annotation { "Feature Type Name" : "Feature", "Feature Type Description" : "" }
export const myFeature = defineFeature(function(context is Context, id is Id, definition is map)
    precondition{}
    {
        {
            var Q0;
            Q0=qCreatedBy(makeId("Top.planeOp"),FACE);
            var sketch = newSketch(context, id + "F0", { "sketchPlane" : qUnion([Q0])});
            skLineSegment(sketch, "E0.bottom", {"start": v(0, 0) * mm, "end": v(19.05, 0) * mm});
            skLineSegment(sketch, "E0.top", {"start": v(0, -63.5) * mm, "end": v(19.05, -63.5) * mm});
            skLineSegment(sketch, "E0.left", {"start": v(0, 0) * mm, "end": v(0, -63.5) * mm});
            skLineSegment(sketch, "E0.right", {"start": v(19.05, 0) * mm, "end": v(19.05, -63.5) * mm});
            skSolve(sketch);
        }
        {
            var Q0;
            Q0=makeQuery(id+"F0.imprint","IMPRINT",FACE,{"disambiguationData":[TD([[makeQuery(id+"F0.imprint","IMPRINT",EDGE,{"derivedFrom":sQuery(id+"F0.wireOp",EDGE,"E0.bottom")}),-1.0]])]});
            extrude(context, id + "F1", {"entities" : qUnion([Q0]), "depth" : 3.8 * mm, "offsetDistance" : 25.4 * mm});
        }
        {
            var Q0;
            Q0=makeQuery(id+"F1.opExtrude","CAP_FACE",FACE,{"disambiguationData":[OSD([sQuery(id+"F0.wireOp",EDGE,"E0.bottom"),sQuery(id+"F0.wireOp",EDGE,"E0.top"),sQuery(id+"F0.wireOp",EDGE,"E0.left"),sQuery(id+"F0.wireOp",EDGE,"E0.right")])],"isStart":false});
            var sketch = newSketch(context, id + "F2", { "sketchPlane" : qUnion([Q0])});
            skLineSegment(sketch, "E1", {"start": v(9.24, -2.12) * mm, "end": v(9.11, -2.05) * mm});
            skLineSegment(sketch, "E2", {"start": v(9.11, -2.05) * mm, "end": v(8.91, -1.97) * mm});
            skLineSegment(sketch, "E3", {"start": v(8.91, -1.97) * mm, "end": v(8.7, -1.89) * mm});
            skLineSegment(sketch, "E4", {"start": v(8.7, -1.89) * mm, "end": v(8.49, -1.82) * mm});
            skLineSegment(sketch, "E5", {"start": v(8.49, -1.82) * mm, "end": v(8.31, -1.76) * mm});
            skLineSegment(sketch, "E6", {"start": v(8.31, -1.76) * mm, "end": v(8.15, -1.7) * mm});
            skLineSegment(sketch, "E7", {"start": v(8.15, -1.7) * mm, "end": v(7.89, -1.66) * mm});
            skLineSegment(sketch, "E8", {"start": v(7.89, -1.66) * mm, "end": v(7.46, -1.56) * mm});
            skLineSegment(sketch, "E9", {"start": v(7.46, -1.56) * mm, "end": v(7.11, -1.51) * mm});
            skPoint(sketch, "E10", {"position": v(6.9, -3.68) * mm});
            skArc(sketch, "E11", {"start": v(7.11, -1.51) * mm, "mid": v(6.21, -1.48) * mm, "end": v(5.33, -1.61) * mm});
            skArc(sketch, "E12", {"start": v(5.33, -1.61) * mm, "mid": v(4.68, -1.82) * mm, "end": v(4.07, -2.09) * mm});
            skArc(sketch, "E13", {"start": v(4.07, -2.09) * mm, "mid": v(3.71, -2.29) * mm, "end": v(3.37, -2.5) * mm});
            skArc(sketch, "E14", {"start": v(3.37, -2.5) * mm, "mid": v(2.87, -2.9) * mm, "end": v(2.44, -3.36) * mm});
            skArc(sketch, "E15", {"start": v(2.44, -3.36) * mm, "mid": v(2.4, -3.4) * mm, "end": v(2.35, -3.45) * mm});
            skArc(sketch, "E16", {"start": v(2.35, -3.45) * mm, "mid": v(2.22, -3.58) * mm, "end": v(2.12, -3.74) * mm});
            skArc(sketch, "E17", {"start": v(2.12, -3.74) * mm, "mid": v(2.1, -3.77) * mm, "end": v(2.07, -3.81) * mm});
            skArc(sketch, "E18", {"start": v(2.07, -3.81) * mm, "mid": v(2.01, -3.9) * mm, "end": v(1.96, -3.98) * mm});
            skArc(sketch, "E19", {"start": v(1.96, -3.98) * mm, "mid": v(1.9, -4.07) * mm, "end": v(1.85, -4.17) * mm});
            skArc(sketch, "E20", {"start": v(1.85, -4.17) * mm, "mid": v(1.78, -4.3) * mm, "end": v(1.72, -4.43) * mm});
            skArc(sketch, "E21", {"start": v(1.72, -4.43) * mm, "mid": v(1.67, -4.54) * mm, "end": v(1.61, -4.65) * mm});
            skArc(sketch, "E22", {"start": v(1.61, -4.65) * mm, "mid": v(1.55, -4.8) * mm, "end": v(1.52, -4.97) * mm});
            skArc(sketch, "E23", {"start": v(1.52, -4.97) * mm, "mid": v(1.5, -5.02) * mm, "end": v(1.5, -5.07) * mm});
            skArc(sketch, "E24", {"start": v(1.5, -5.07) * mm, "mid": v(1.46, -5.18) * mm, "end": v(1.45, -5.3) * mm});
            skArc(sketch, "E25", {"start": v(1.45, -5.3) * mm, "mid": v(1.44, -5.37) * mm, "end": v(1.43, -5.44) * mm});
            skArc(sketch, "E26", {"start": v(1.43, -5.44) * mm, "mid": v(1.4, -5.59) * mm, "end": v(1.4, -5.74) * mm});
            skArc(sketch, "E27", {"start": v(1.4, -5.74) * mm, "mid": v(1.4, -5.8) * mm, "end": v(1.4, -5.85) * mm});
            skArc(sketch, "E28", {"start": v(1.4, -5.85) * mm, "mid": v(1.4, -6.03) * mm, "end": v(1.4, -6.2) * mm});
            skArc(sketch, "E29", {"start": v(1.4, -6.2) * mm, "mid": v(1.44, -6.41) * mm, "end": v(1.47, -6.62) * mm});
            skArc(sketch, "E30", {"start": v(1.47, -6.62) * mm, "mid": v(1.53, -6.86) * mm, "end": v(1.62, -7.1) * mm});
            skArc(sketch, "E31", {"start": v(1.62, -7.1) * mm, "mid": v(1.67, -7.2) * mm, "end": v(1.7, -7.33) * mm});
            skLineSegment(sketch, "E32", {"start": v(1.7, -7.33) * mm, "end": v(1.8, -7.51) * mm});
            skLineSegment(sketch, "E33", {"start": v(1.8, -7.51) * mm, "end": v(1.9, -7.7) * mm});
            skLineSegment(sketch, "E34", {"start": v(1.9, -7.7) * mm, "end": v(2, -7.84) * mm});
            skLineSegment(sketch, "E35", {"start": v(2, -7.84) * mm, "end": v(2.08, -7.98) * mm});
            skLineSegment(sketch, "E36", {"start": v(2.08, -7.98) * mm, "end": v(2.28, -8.24) * mm});
            skLineSegment(sketch, "E37", {"start": v(2.28, -8.24) * mm, "end": v(2.43, -8.4) * mm});
            skLineSegment(sketch, "E38", {"start": v(2.43, -8.4) * mm, "end": v(2.56, -8.55) * mm});
            skLineSegment(sketch, "E39", {"start": v(2.56, -8.55) * mm, "end": v(2.73, -8.7) * mm});
            skLineSegment(sketch, "E40", {"start": v(2.73, -8.7) * mm, "end": v(2.94, -8.89) * mm});
            skLineSegment(sketch, "E41", {"start": v(2.94, -8.89) * mm, "end": v(3.14, -9.03) * mm});
            skLineSegment(sketch, "E42", {"start": v(3.14, -9.03) * mm, "end": v(3.36, -9.18) * mm});
            skLineSegment(sketch, "E43", {"start": v(3.36, -9.18) * mm, "end": v(3.53, -9.29) * mm});
            skLineSegment(sketch, "E44", {"start": v(3.53, -9.29) * mm, "end": v(3.68, -9.37) * mm});
            skLineSegment(sketch, "E45", {"start": v(3.68, -9.37) * mm, "end": v(4, -9.51) * mm});
            skLineSegment(sketch, "E46", {"start": v(4, -9.51) * mm, "end": v(4.22, -9.6) * mm});
            skLineSegment(sketch, "E47", {"start": v(4.22, -9.6) * mm, "end": v(4.41, -9.68) * mm});
            skLineSegment(sketch, "E48", {"start": v(4.41, -9.68) * mm, "end": v(4.6, -9.74) * mm});
            skLineSegment(sketch, "E49", {"start": v(4.6, -9.74) * mm, "end": v(4.8, -9.8) * mm});
            skLineSegment(sketch, "E50", {"start": v(4.8, -9.8) * mm, "end": v(4.96, -9.83) * mm});
            skArc(sketch, "E51", {"start": v(4.96, -9.83) * mm, "mid": v(4.97, -9.84) * mm, "end": v(4.98, -9.84) * mm});
            skArc(sketch, "E52", {"start": v(4.98, -9.84) * mm, "mid": v(5.08, -9.87) * mm, "end": v(5.18, -9.89) * mm});
            skArc(sketch, "E53", {"start": v(5.18, -9.89) * mm, "mid": v(5.2, -9.89) * mm, "end": v(5.22, -9.9) * mm});
            skArc(sketch, "E54", {"start": v(5.22, -9.9) * mm, "mid": v(5.28, -9.9) * mm, "end": v(5.35, -9.91) * mm});
            skLineSegment(sketch, "E55", {"start": v(5.35, -9.91) * mm, "end": v(5.48, -9.93) * mm});
            skLineSegment(sketch, "E56", {"start": v(5.48, -9.93) * mm, "end": v(5.67, -9.96) * mm});
            skLineSegment(sketch, "E57", {"start": v(5.67, -9.96) * mm, "end": v(5.78, -9.97) * mm});
            skLineSegment(sketch, "E58", {"start": v(5.78, -9.97) * mm, "end": v(5.94, -9.99) * mm});
            skLineSegment(sketch, "E59", {"start": v(5.94, -9.99) * mm, "end": v(6.45, -9.99) * mm});
            skArc(sketch, "E60", {"start": v(6.45, -9.99) * mm, "mid": v(7.31, -9.94) * mm, "end": v(8.16, -9.78) * mm});
            skArc(sketch, "E61", {"start": v(8.16, -9.78) * mm, "mid": v(8.89, -9.57) * mm, "end": v(9.59, -9.3) * mm});
            skLineSegment(sketch, "E62", {"start": v(9.59, -9.3) * mm, "end": v(9.59, -9.52) * mm});
            skLineSegment(sketch, "E63", {"start": v(9.59, -9.52) * mm, "end": v(11.4, -9.52) * mm});
            skLineSegment(sketch, "E64", {"start": v(11.4, -9.52) * mm, "end": v(11.4, -6.58) * mm});
            skLineSegment(sketch, "E65", {"start": v(11.4, -6.58) * mm, "end": v(11.89, -6.58) * mm});
            skLineSegment(sketch, "E66", {"start": v(11.89, -6.58) * mm, "end": v(11.89, -9.87) * mm});
            skLineSegment(sketch, "E67", {"start": v(11.89, -9.87) * mm, "end": v(10.96, -9.87) * mm});
            skLineSegment(sketch, "E68", {"start": v(10.96, -9.87) * mm, "end": v(10.96, -11.56) * mm});
            skLineSegment(sketch, "E69", {"start": v(10.96, -11.56) * mm, "end": v(14.98, -11.56) * mm});
            skLineSegment(sketch, "E70", {"start": v(14.98, -11.56) * mm, "end": v(14.98, -9.87) * mm});
            skLineSegment(sketch, "E71", {"start": v(14.98, -9.87) * mm, "end": v(14.12, -9.87) * mm});
            skLineSegment(sketch, "E72", {"start": v(14.12, -9.87) * mm, "end": v(14.12, -6.58) * mm});
            skLineSegment(sketch, "E73", {"start": v(14.12, -6.58) * mm, "end": v(16, -6.58) * mm});
            skLineSegment(sketch, "E74", {"start": v(16, -6.58) * mm, "end": v(16.14, -7.3) * mm});
            skLineSegment(sketch, "E75", {"start": v(16.14, -7.3) * mm, "end": v(17.66, -7.3) * mm});
            skLineSegment(sketch, "E76", {"start": v(17.66, -7.3) * mm, "end": v(17.66, -4.7) * mm});
            skLineSegment(sketch, "E77", {"start": v(17.66, -4.7) * mm, "end": v(7.77, -4.7) * mm});
            skLineSegment(sketch, "E78", {"start": v(7.77, -4.7) * mm, "end": v(7.77, -7.3) * mm});
            skLineSegment(sketch, "E79", {"start": v(7.77, -7.3) * mm, "end": v(9.28, -7.3) * mm});
            skLineSegment(sketch, "E80", {"start": v(9.28, -7.3) * mm, "end": v(9.4, -6.58) * mm});
            skLineSegment(sketch, "E81", {"start": v(9.4, -6.58) * mm, "end": v(9.83, -6.58) * mm});
            skLineSegment(sketch, "E82", {"start": v(9.83, -6.58) * mm, "end": v(9.75, -6.83) * mm});
            skLineSegment(sketch, "E83", {"start": v(9.75, -6.83) * mm, "end": v(9.62, -7.1) * mm});
            skLineSegment(sketch, "E84", {"start": v(9.62, -7.1) * mm, "end": v(9.52, -7.25) * mm});
            skLineSegment(sketch, "E85", {"start": v(9.52, -7.25) * mm, "end": v(9.35, -7.47) * mm});
            skLineSegment(sketch, "E86", {"start": v(9.35, -7.47) * mm, "end": v(9.28, -7.55) * mm});
            skLineSegment(sketch, "E87", {"start": v(9.28, -7.55) * mm, "end": v(9.1, -7.73) * mm});
            skLineSegment(sketch, "E88", {"start": v(9.1, -7.73) * mm, "end": v(9, -7.8) * mm});
            skLineSegment(sketch, "E89", {"start": v(9, -7.8) * mm, "end": v(8.84, -7.92) * mm});
            skLineSegment(sketch, "E90", {"start": v(8.84, -7.92) * mm, "end": v(8.76, -7.96) * mm});
            skLineSegment(sketch, "E91", {"start": v(8.76, -7.96) * mm, "end": v(8.68, -8) * mm});
            skLineSegment(sketch, "E92", {"start": v(8.68, -8) * mm, "end": v(8.54, -8.07) * mm});
            skLineSegment(sketch, "E93", {"start": v(8.54, -8.07) * mm, "end": v(8.46, -8.1) * mm});
            skLineSegment(sketch, "E94", {"start": v(8.46, -8.1) * mm, "end": v(8.34, -8.15) * mm});
            skLineSegment(sketch, "E95", {"start": v(8.34, -8.15) * mm, "end": v(8.26, -8.18) * mm});
            skLineSegment(sketch, "E96", {"start": v(8.26, -8.18) * mm, "end": v(8.18, -8.2) * mm});
            skLineSegment(sketch, "E97", {"start": v(8.18, -8.2) * mm, "end": v(8.1, -8.23) * mm});
            skLineSegment(sketch, "E98", {"start": v(8.1, -8.23) * mm, "end": v(8.02, -8.24) * mm});
            skLineSegment(sketch, "E99", {"start": v(8.02, -8.24) * mm, "end": v(7.91, -8.26) * mm});
            skLineSegment(sketch, "E100", {"start": v(7.91, -8.26) * mm, "end": v(7.8, -8.29) * mm});
            skLineSegment(sketch, "E101", {"start": v(7.8, -8.29) * mm, "end": v(7.51, -8.32) * mm});
            skLineSegment(sketch, "E102", {"start": v(7.51, -8.32) * mm, "end": v(7.41, -8.32) * mm});
            skLineSegment(sketch, "E103", {"start": v(7.41, -8.32) * mm, "end": v(7.1, -8.32) * mm});
            skLineSegment(sketch, "E104", {"start": v(7.1, -8.32) * mm, "end": v(6.94, -8.32) * mm});
            skLineSegment(sketch, "E105", {"start": v(6.94, -8.32) * mm, "end": v(6.83, -8.32) * mm});
            skLineSegment(sketch, "E106", {"start": v(6.83, -8.32) * mm, "end": v(6.8, -8.32) * mm});
            skPoint(sketch, "E106.endSnap0", {"position": v(6.88, -8.32) * mm});
            skLineSegment(sketch, "E107", {"start": v(6.8, -8.32) * mm, "end": v(6.67, -8.32) * mm});
            skLineSegment(sketch, "E108", {"start": v(6.67, -8.32) * mm, "end": v(6.44, -8.3) * mm});
            skLineSegment(sketch, "E109", {"start": v(6.44, -8.3) * mm, "end": v(6.16, -8.23) * mm});
            skLineSegment(sketch, "E110", {"start": v(6.16, -8.23) * mm, "end": v(5.92, -8.17) * mm});
            skLineSegment(sketch, "E111", {"start": v(5.92, -8.17) * mm, "end": v(5.68, -8.08) * mm});
            skLineSegment(sketch, "E112", {"start": v(5.68, -8.08) * mm, "end": v(5.58, -8.04) * mm});
            skLineSegment(sketch, "E113", {"start": v(5.58, -8.04) * mm, "end": v(5.46, -7.99) * mm});
            skLineSegment(sketch, "E114", {"start": v(5.46, -7.99) * mm, "end": v(5.2, -7.84) * mm});
            skLineSegment(sketch, "E115", {"start": v(5.2, -7.84) * mm, "end": v(5.06, -7.76) * mm});
            skLineSegment(sketch, "E116", {"start": v(5.06, -7.76) * mm, "end": v(4.87, -7.62) * mm});
            skLineSegment(sketch, "E117", {"start": v(4.87, -7.62) * mm, "end": v(4.76, -7.53) * mm});
            skLineSegment(sketch, "E118", {"start": v(4.76, -7.53) * mm, "end": v(4.6, -7.4) * mm});
            skLineSegment(sketch, "E119", {"start": v(4.6, -7.4) * mm, "end": v(4.55, -7.33) * mm});
            skLineSegment(sketch, "E120", {"start": v(4.55, -7.33) * mm, "end": v(4.49, -7.26) * mm});
            skLineSegment(sketch, "E121", {"start": v(4.49, -7.26) * mm, "end": v(4.42, -7.17) * mm});
            skArc(sketch, "E122", {"start": v(4.42, -7.17) * mm, "mid": v(4.07, -6.5) * mm, "end": v(4, -5.73) * mm});
            skArc(sketch, "E123", {"start": v(4, -5.73) * mm, "mid": v(4.13, -5.19) * mm, "end": v(4.36, -4.68) * mm});
            skArc(sketch, "E124", {"start": v(4.36, -4.68) * mm, "mid": v(5, -3.96) * mm, "end": v(5.87, -3.53) * mm});
            skArc(sketch, "E125", {"start": v(5.87, -3.53) * mm, "mid": v(6.44, -3.4) * mm, "end": v(7.02, -3.33) * mm});
            skArc(sketch, "E126", {"start": v(7.02, -3.33) * mm, "mid": v(7.5, -3.35) * mm, "end": v(7.98, -3.47) * mm});
            skArc(sketch, "E127", {"start": v(7.98, -3.47) * mm, "mid": v(8.36, -3.61) * mm, "end": v(8.74, -3.77) * mm});
            skArc(sketch, "E128", {"start": v(8.74, -3.77) * mm, "mid": v(8.92, -3.87) * mm, "end": v(9.1, -3.98) * mm});
            skArc(sketch, "E129", {"start": v(9.1, -3.98) * mm, "mid": v(9.36, -4.17) * mm, "end": v(9.63, -4.37) * mm});
            skLineSegment(sketch, "E130", {"start": v(9.63, -4.37) * mm, "end": v(11.26, -4.37) * mm});
            skLineSegment(sketch, "E131", {"start": v(11.26, -4.37) * mm, "end": v(11.26, -1.49) * mm});
            skLineSegment(sketch, "E132", {"start": v(11.26, -1.49) * mm, "end": v(9.54, -1.49) * mm});
            skLineSegment(sketch, "E133", {"start": v(9.54, -1.49) * mm, "end": v(9.54, -2.26) * mm});
            skLineSegment(sketch, "E134", {"start": v(9.24, -2.12) * mm, "end": v(9.54, -2.26) * mm});
            skSolve(sketch);
        }
        {
            var Q0;
            Q0 = qSketchRegion(id + "F2", true);
            extrude(context, id + "F3", {"entities" : qUnion([Q0]), "operationType" : NewBodyOperationType.REMOVE, "oppositeDirection" : true, "depth" : 6.35 * mm, "offsetDistance" : 25.4 * mm});
        }
        {
            var Q0;
            Q0=makeQuery(id+"F1.opExtrude","CAP_FACE",FACE,{"disambiguationData":[OSD([sQuery(id+"F0.wireOp",EDGE,"E0.bottom"),sQuery(id+"F0.wireOp",EDGE,"E0.top"),sQuery(id+"F0.wireOp",EDGE,"E0.left"),sQuery(id+"F0.wireOp",EDGE,"E0.right")])],"isStart":false});
            var sketch = newSketch(context, id + "F4", { "sketchPlane" : qUnion([Q0])});
            skText(sketch, "E135", { "text": "Jefferson Edge", "fontName": "OpenSans-Regular.ttf"});
            const initialGuessF4  = {"E135": [0.00686, -0.01525, 0, -1, 0.00457]};
            skSetInitialGuess(sketch, initialGuessF4);
            skSolve(sketch);
        }
        {
            var Q0;
            Q0 = qSketchRegion(id + "F4", true);
            extrude(context, id + "F5", {"entities" : qUnion([Q0]), "operationType" : NewBodyOperationType.REMOVE, "oppositeDirection" : true, "depth" : 2.54 * mm, "offsetDistance" : 25.4 * mm});
        }
        {
            var Q0;
            Q0=makeQuery(id+"F1.opExtrude","SWEPT_EDGE",EDGE,{"disambiguationData":[OSD([sQuery(id+"F0.wireOp",EDGE,"E0.top"),sQuery(id+"F0.wireOp",EDGE,"E0.right")])]});
            var Q1;
            Q1=makeQuery(id+"F1.opExtrude","SWEPT_EDGE",EDGE,{"disambiguationData":[OSD([sQuery(id+"F0.wireOp",EDGE,"E0.top"),sQuery(id+"F0.wireOp",EDGE,"E0.left")])]});
            chamfer(context, id + "F6", {"entities" : qUnion([Q0, Q1]), "width" : 5.08 * mm, "tangentPropagation" : true});
        }
        {
            var Q0;
            Q0=makeQuery(id+"F1.opExtrude","SWEPT_EDGE",EDGE,{"disambiguationData":[OSD([sQuery(id+"F0.wireOp",EDGE,"E0.bottom"),sQuery(id+"F0.wireOp",EDGE,"E0.left")])]});
            var Q1;
            Q1=makeQuery(id+"F1.opExtrude","SWEPT_EDGE",EDGE,{"disambiguationData":[OSD([sQuery(id+"F0.wireOp",EDGE,"E0.bottom"),sQuery(id+"F0.wireOp",EDGE,"E0.right")])]});
            fillet(context, id + "F7", {"entities" : qUnion([Q0, Q1]), "radius" : 5.08 * mm, "tangentPropagation" : true, "allowEdgeOverflow" : false});
        }
        {
            var Q0;
            Q0=makeQuery(id+"F1.opExtrude","SWEPT_FACE",FACE,{"disambiguationData":[OSD([sQuery(id+"F0.wireOp",EDGE,"E0.bottom")])]});
            extrude(context, id + "F8", {"entities" : qUnion([Q0]), "operationType" : NewBodyOperationType.ADD, "depth" : 3.8 * mm, "offsetDistance" : 25.4 * mm});
        }
        {
            var Q0;
            {var subQ0=sQuery(id+"F0.wireOp",EDGE,"E0.bottom");var subQ1=sQuery(id+"F0.wireOp",EDGE,"E0.top");var subQ2=sQuery(id+"F0.wireOp",EDGE,"E0.right");var subQ3=sQuery(id+"F0.wireOp",EDGE,"E0.left");Q0=makeQuery(id+"F8.boolean.opBoolean","MERGE",FACE,{"derivedFrom":[makeQuery(id+"F5.boolean.opBoolean","SPLIT",FACE,{"disambiguationData":[TD([makeQuery(id+"F1.opExtrude","SWEPT_FACE",FACE,{"disambiguationData":[OSD([subQ0])]})])],"derivedFrom":makeQuery(id+"F1.opExtrude","CAP_FACE",FACE,{"disambiguationData":[OSD([subQ0,subQ1,subQ3,subQ2])],"isStart":false})}),makeQuery(id+"F8.opExtrude","SWEPT_FACE",FACE,{"disambiguationData":[OSD([subQ0]),TDD([makeQuery(id+"F1.opExtrude","CAP_EDGE",EDGE,{"disambiguationData":[OSD([subQ0])],"isStart":false})])]})]});}
            var sketch = newSketch(context, id + "F9", { "sketchPlane" : qUnion([Q0])});
            skCircle(sketch, "E136", {"center": v(9.46, 1.9) * mm, "radius": 1.27 * mm});
            skLineSegment(sketch, "E137", {"start": v(5.08, 0) * mm, "end": v(13.97, 0) * mm});
            skSolve(sketch);
        }
        {
            var Q0;
            Q0 = qSketchRegion(id + "F9", true);
            var Q1;
            Q1=makeQuery(id+"F9.imprint","IMPRINT",FACE,{"disambiguationData":[TD([[makeQuery(id+"F9.imprint","IMPRINT",EDGE,{"derivedFrom":sQuery(id+"F9.wireOp",EDGE,"E136")}),1.0]])]});
            extrude(context, id + "F10", {"entities" : qUnion([Q0, Q1]), "operationType" : NewBodyOperationType.REMOVE, "oppositeDirection" : true, "depth" : 25.4 * mm, "offsetDistance" : 25.4 * mm});
        }
    });